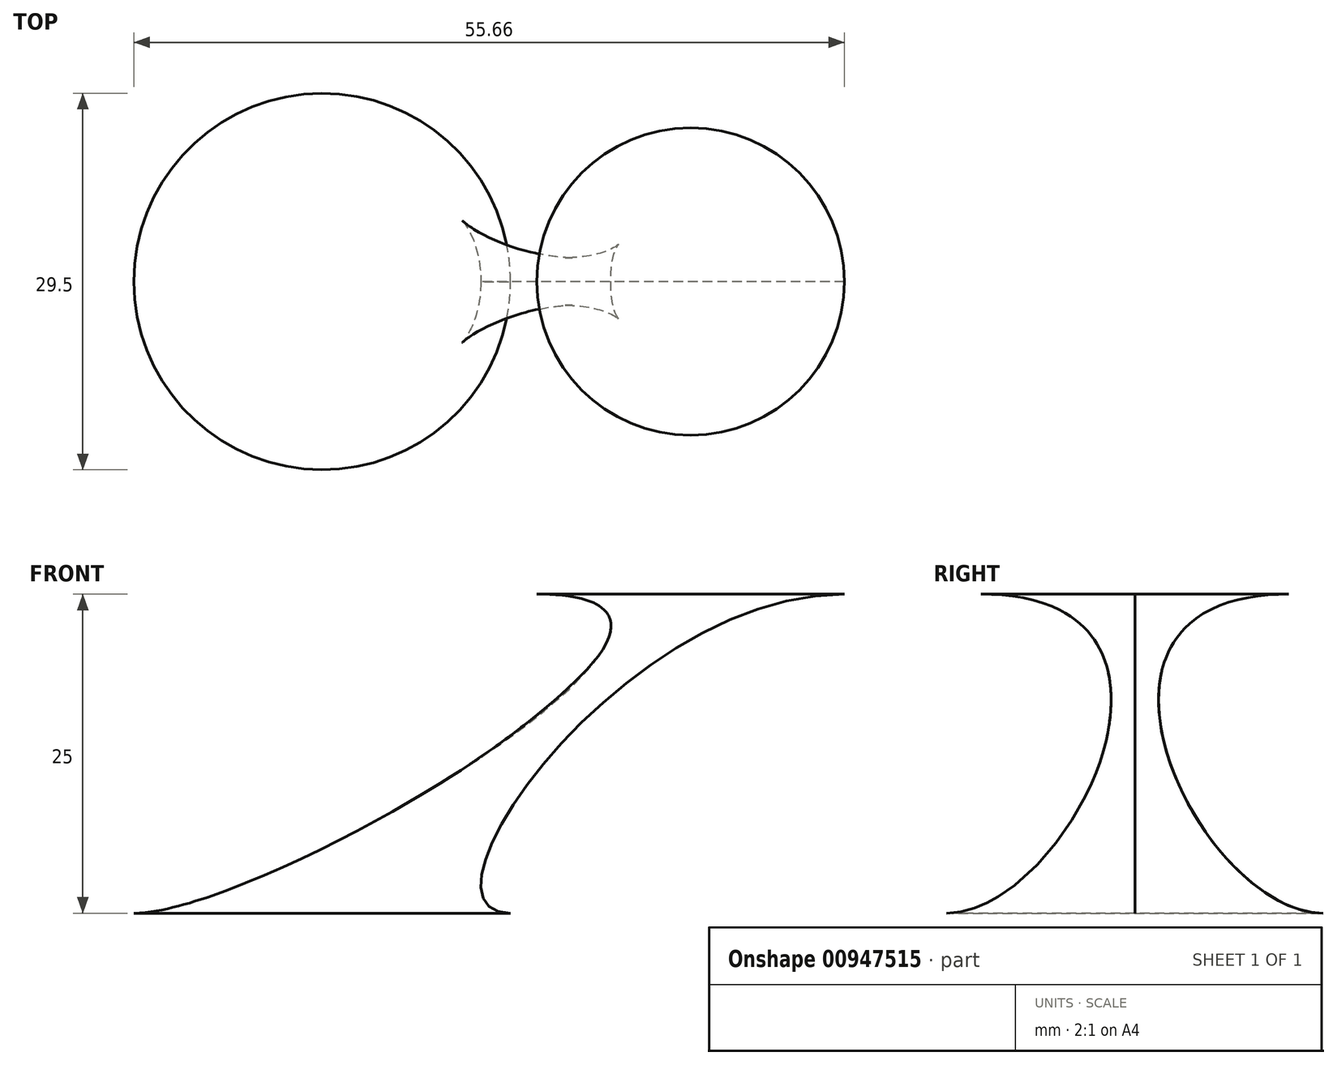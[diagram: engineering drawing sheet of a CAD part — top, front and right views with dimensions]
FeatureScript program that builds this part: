
annotation { "Feature Type Name" : "Feature", "Feature Type Description" : "" }
export const myFeature = defineFeature(function(context is Context, id is Id, definition is map)
    precondition{}
    {
        {
            var Q0;
            Q0=qCreatedBy(makeId("Top.planeOp"),FACE);
            cPlane(context, id + "F0", {"entities" : qUnion([Q0]), "cplaneType" : CPlaneType.OFFSET, "offset" : 25 * mm, "width" : 150 * mm, "height" : 150 * mm});
        }
        {
            var Q0;
            Q0=qCreatedBy(makeId("Top.planeOp"),FACE);
            var sketch = newSketch(context, id + "F1", { "sketchPlane" : qUnion([Q0])});
            skCircle(sketch, "E0", {"center": v(0, 0) * mm, "radius": 14.75 * mm});
            skSolve(sketch);
        }
        {
            var Q0;
            Q0=qCreatedBy(id+"F0.planeOp",FACE);
            var sketch = newSketch(context, id + "F2", { "sketchPlane" : qUnion([Q0])});
            skCircle(sketch, "E1", {"center": v(28.86, 0) * mm, "radius": 12.05 * mm});
            skSolve(sketch);
        }
        {
            var Q0;
            Q0 = qSketchRegion(id + "F2", true);
            var Q1;
            Q1 = qSketchRegion(id + "F1", true);
            loft(context, id + "F3", {"sheetProfilesArray" : [{ "sheetProfileEntities" : qUnion([Q0]) }, { "sheetProfileEntities" : qUnion([Q1]) }], "startCondition" : LoftEndDerivativeType.TANGENT_TO_PROFILE, "startMagnitude" : 2, "endCondition" : LoftEndDerivativeType.TANGENT_TO_PROFILE, "endMagnitude" : -1});
        }
    });
